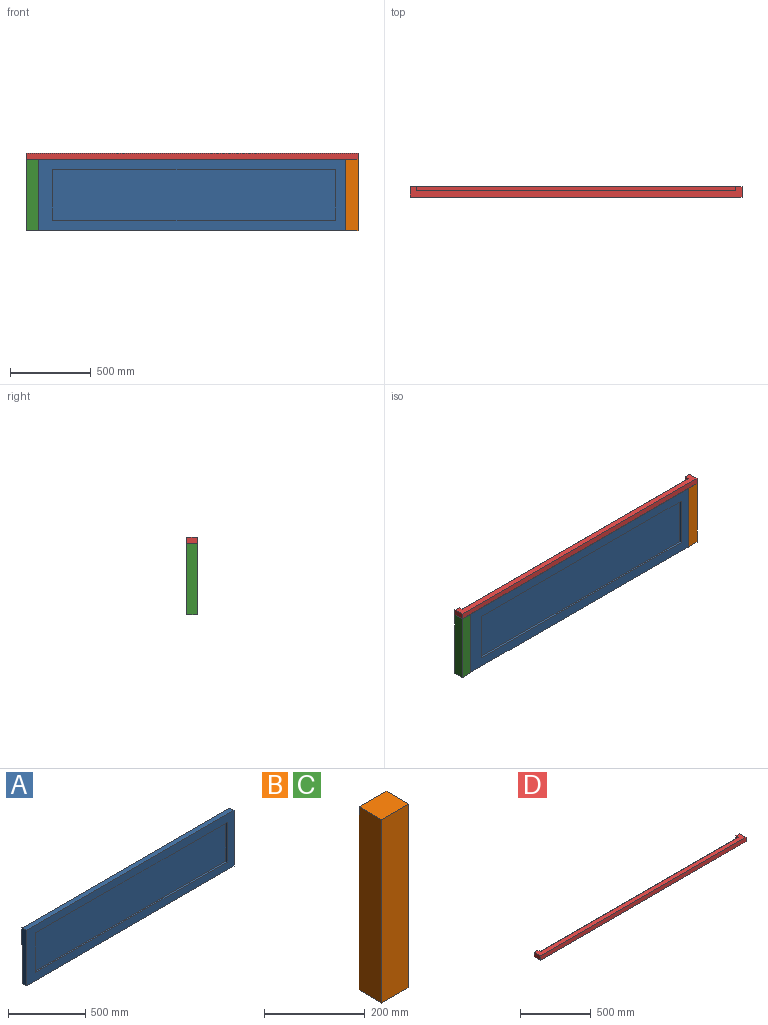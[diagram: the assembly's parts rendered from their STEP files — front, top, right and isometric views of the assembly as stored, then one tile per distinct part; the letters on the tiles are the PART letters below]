
ASSEMBLY  parts=4 mates=9
PART A: 11 faces, bbox 1905x38.1x441.3 mm
  f0: plane 1905x441.33mm, normal (0,-1,0), area 289838.1mm2, adj f1,f2,f3,f4,f6,f7,f8,f9
  f1: plane 441.33x38.1mm, normal (-1,0,0), area 16814.5mm2, adj f0,f2,f4,f5
  f2: plane 1905x38.1mm, normal (0,0,-1), area 72580.5mm2, adj f0,f1,f3,f5
  f3: plane 441.33x38.1mm, normal (1,0,0), area 16814.5mm2, adj f0,f2,f4,f5
  f4: plane 1905x38.1mm, normal (0,0,1), area 72580.5mm2, adj f0,f1,f3,f5
  f5: plane 1905x441.33mm, normal (0,1,0), area 840724.1mm2, adj f1,f2,f3,f4
  f6: plane 1752.6x12.7mm, normal (0,0,-1), area 22258mm2, adj f0,f7,f9,f10
  f7: plane 314.33x12.7mm, normal (1,0,0), area 3991.9mm2, adj f0,f6,f8,f10
  f8: plane 1752.6x12.7mm, normal (0,0,1), area 22258mm2, adj f0,f7,f9,f10
  f9: plane 314.33x12.7mm, normal (-1,0,0), area 3991.9mm2, adj f0,f6,f8,f10
  f10: plane 1752.6x314.33mm, normal (0,-1,0), area 550886mm2, adj f6,f7,f8,f9
PART B: 6 faces, bbox 76.2x63.5x444.5 mm
  f0: plane 444.5x63.5mm, normal (-1,0,0), area 28225.8mm2, adj f1,f3,f4,f5
  f1: plane 444.5x76.2mm, normal (0,-1,0), area 33870.9mm2, adj f0,f2,f4,f5
  f2: plane 444.5x63.5mm, normal (1,0,0), area 28225.8mm2, adj f1,f3,f4,f5
  f3: plane 444.5x76.2mm, normal (0,1,0), area 33870.9mm2, adj f0,f2,f4,f5
  f4: plane 76.2x63.5mm, normal (0,0,1), area 4838.7mm2, adj f0,f1,f2,f3
  f5: plane 76.2x63.5mm, normal (0,0,-1), area 4838.7mm2, adj f0,f1,f2,f3
PART C: same geometry as B
PART D: 10 faces, bbox 2057.4x63.5x38.1 mm
  f0: plane 2057.4x38.1mm, normal (0,1,0), area 28064.5mm2, adj f1,f3,f4,f5,f6,f8,f9
  f1: plane 63.5x38.1mm, normal (-1,0,0), area 2419.3mm2, adj f0,f2,f4,f5
  f2: plane 2057.4x38.1mm, normal (0,-1,0), area 78386.9mm2, adj f1,f3,f4,f5
  f3: plane 63.5x38.1mm, normal (1,0,0), area 2419.3mm2, adj f0,f2,f4,f5
  f4: plane 2057.4x63.5mm, normal (0,0,1), area 80322.4mm2, adj f0,f1,f2,f3,f6,f7,f8
  f5: plane 2057.4x63.5mm, normal (0,0,-1), area 130644.9mm2, adj f0,f1,f2,f3
  f6: plane 25.4x25.4mm, normal (1,0,0), area 645.2mm2, adj f0,f4,f7,f9
  f7: plane 1981.2x25.4mm, normal (0,1,0), area 50322.5mm2, adj f4,f6,f8,f9
  f8: plane 25.4x25.4mm, normal (-1,0,0), area 645.2mm2, adj f0,f4,f7,f9
  f9: plane 1981.2x25.4mm, normal (0,0,1), area 50322.5mm2, adj f0,f6,f7,f8
PLACE A t=(672.64,53.01,1.59)mm
PLACE B t=(2577.64,12.7,-1.59)mm
PLACE C t=(596.44,12.7,-1.59)mm
PLACE D t=(596.44,14.91,442.91)mm
MATE planar B.f1 <-> C.f1  axis (0,-1,0) through (2615.74,14.91,220.66)mm
MATE planar A.f3 <-> B.f0  axis (1,0,0) through (2577.64,33.96,222.25)mm
MATE planar D.f2 <-> C.f1  axis (0,-1,0) through (1625.14,14.91,461.96)mm
MATE planar D.f1 <-> C.f0  axis (-1,0,0) through (596.44,46.66,461.96)mm
MATE planar D.f5 <-> C.f4  axis (0,0,-1) through (1625.14,46.66,442.91)mm
MATE planar B.f4 <-> A.f4  axis (0,0,1) through (2615.74,46.66,442.91)mm
MATE planar A.f0 <-> C.f1  axis (0,-1,0) through (761.54,14.91,379.41)mm
MATE planar A.f4 <-> C.f4  axis (0,0,1) through (1625.14,33.96,442.91)mm
MATE planar A.f1 <-> C.f2  axis (-1,0,0) through (672.64,33.96,222.25)mm
